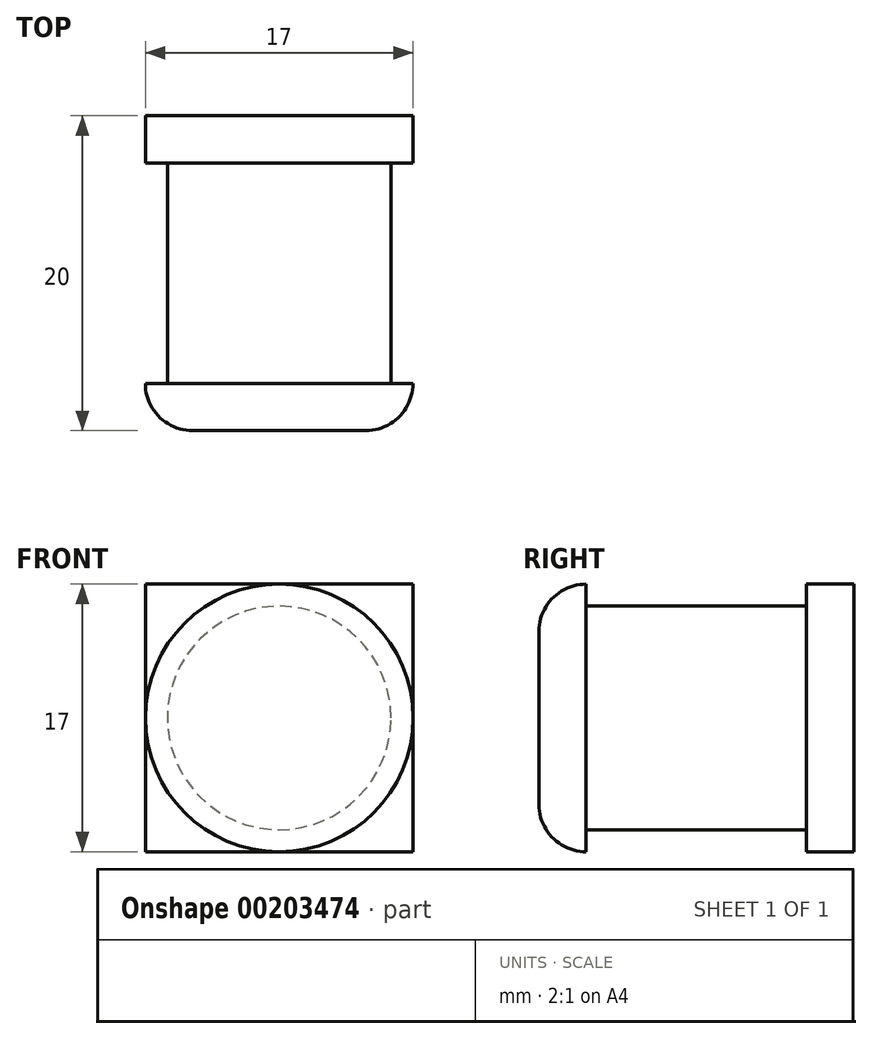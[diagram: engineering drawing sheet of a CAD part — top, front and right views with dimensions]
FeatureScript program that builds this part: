
annotation { "Feature Type Name" : "Feature", "Feature Type Description" : "" }
export const myFeature = defineFeature(function(context is Context, id is Id, definition is map)
    precondition{}
    {
        {
            var Q0;
            Q0=qCreatedBy(makeId("Front.planeOp"),FACE);
            var sketch = newSketch(context, id + "F0", { "sketchPlane" : qUnion([Q0])});
            skCircle(sketch, "E0", {"center": v(0, 0) * mm, "radius": 7.1 * mm});
            skSolve(sketch);
        }
        {
            var Q0;
            Q0=makeQuery(id+"F0.imprint","IMPRINT",FACE,{"disambiguationData":[TD([[makeQuery(id+"F0.imprint","IMPRINT",EDGE,{"derivedFrom":sQuery(id+"F0.wireOp",EDGE,"E0")}),1.0]])]});
            extrude(context, id + "F1", {"entities" : qUnion([Q0]), "depth" : 14 * mm});
        }
        {
            var Q0;
            Q0=makeQuery(id+"F1.opExtrude","CAP_FACE",FACE,{"disambiguationData":[OSD([sQuery(id+"F0.wireOp",EDGE,"E0")])],"isStart":false});
            var sketch = newSketch(context, id + "F2", { "sketchPlane" : qUnion([Q0])});
            skCircle(sketch, "E1", {"center": v(0, 0) * mm, "radius": 8.5 * mm});
            skSolve(sketch);
        }
        {
            var Q0;
            Q0=makeQuery(id+"F2.imprint","IMPRINT",FACE,{"disambiguationData":[TD([[makeQuery(id+"F2.imprint","IMPRINT",EDGE,{"derivedFrom":sQuery(id+"F2.wireOp",EDGE,"E1")}),1.0]])]});
            var Q1;
            Q1=makeQuery(id+"F2.imprint","IMPRINT",FACE,{"disambiguationData":[TD([[makeQuery(id+"F2.imprint","IMPRINT",EDGE,{"derivedFrom":makeQuery(id+"F1.opExtrude","CAP_EDGE",EDGE,{"disambiguationData":[OSD([sQuery(id+"F0.wireOp",EDGE,"E0")])],"isStart":false})}),1.0]])]});
            extrude(context, id + "F3", {"entities" : qUnion([Q0, Q1]), "operationType" : NewBodyOperationType.ADD, "depth" : 3 * mm});
        }
        {
            var Q0;
            Q0=makeQuery(id+"F3.opExtrude","CAP_EDGE",EDGE,{"disambiguationData":[OSD([sQuery(id+"F2.wireOp",EDGE,"E1")])],"isStart":false});
            fillet(context, id + "F4", {"entities" : qUnion([Q0]), "radius" : 3 * mm, "tangentPropagation" : true, "allowEdgeOverflow" : false});
        }
        {
            var Q0;
            Q0=makeQuery(id+"F1.opExtrude","CAP_FACE",FACE,{"disambiguationData":[OSD([sQuery(id+"F0.wireOp",EDGE,"E0")])],"isStart":true});
            var sketch = newSketch(context, id + "F5", { "sketchPlane" : qUnion([Q0])});
            skLineSegment(sketch, "E2.bottom", {"start": v(-8.5, 8.5) * mm, "end": v(8.5, 8.5) * mm});
            skLineSegment(sketch, "E2.top", {"start": v(-8.5, -8.5) * mm, "end": v(8.5, -8.5) * mm});
            skLineSegment(sketch, "E2.left", {"start": v(-8.5, 8.5) * mm, "end": v(-8.5, -8.5) * mm});
            skLineSegment(sketch, "E2.right", {"start": v(8.5, 8.5) * mm, "end": v(8.5, -8.5) * mm});
            skSolve(sketch);
        }
        {
            var Q0;
            Q0=makeQuery(id+"F5.imprint","IMPRINT",FACE,{"disambiguationData":[TD([[makeQuery(id+"F5.imprint","IMPRINT",EDGE,{"derivedFrom":sQuery(id+"F5.wireOp",EDGE,"E2.bottom")}),-1.0]])]});
            var Q1;
            Q1=makeQuery(id+"F5.imprint","IMPRINT",FACE,{"disambiguationData":[TD([[makeQuery(id+"F5.imprint","IMPRINT",EDGE,{"derivedFrom":makeQuery(id+"F1.opExtrude","CAP_EDGE",EDGE,{"disambiguationData":[OSD([sQuery(id+"F0.wireOp",EDGE,"E0")])],"isStart":true})}),-1.0]])]});
            extrude(context, id + "F6", {"entities" : qUnion([Q0, Q1]), "operationType" : NewBodyOperationType.ADD, "depth" : 3 * mm});
        }
    });
